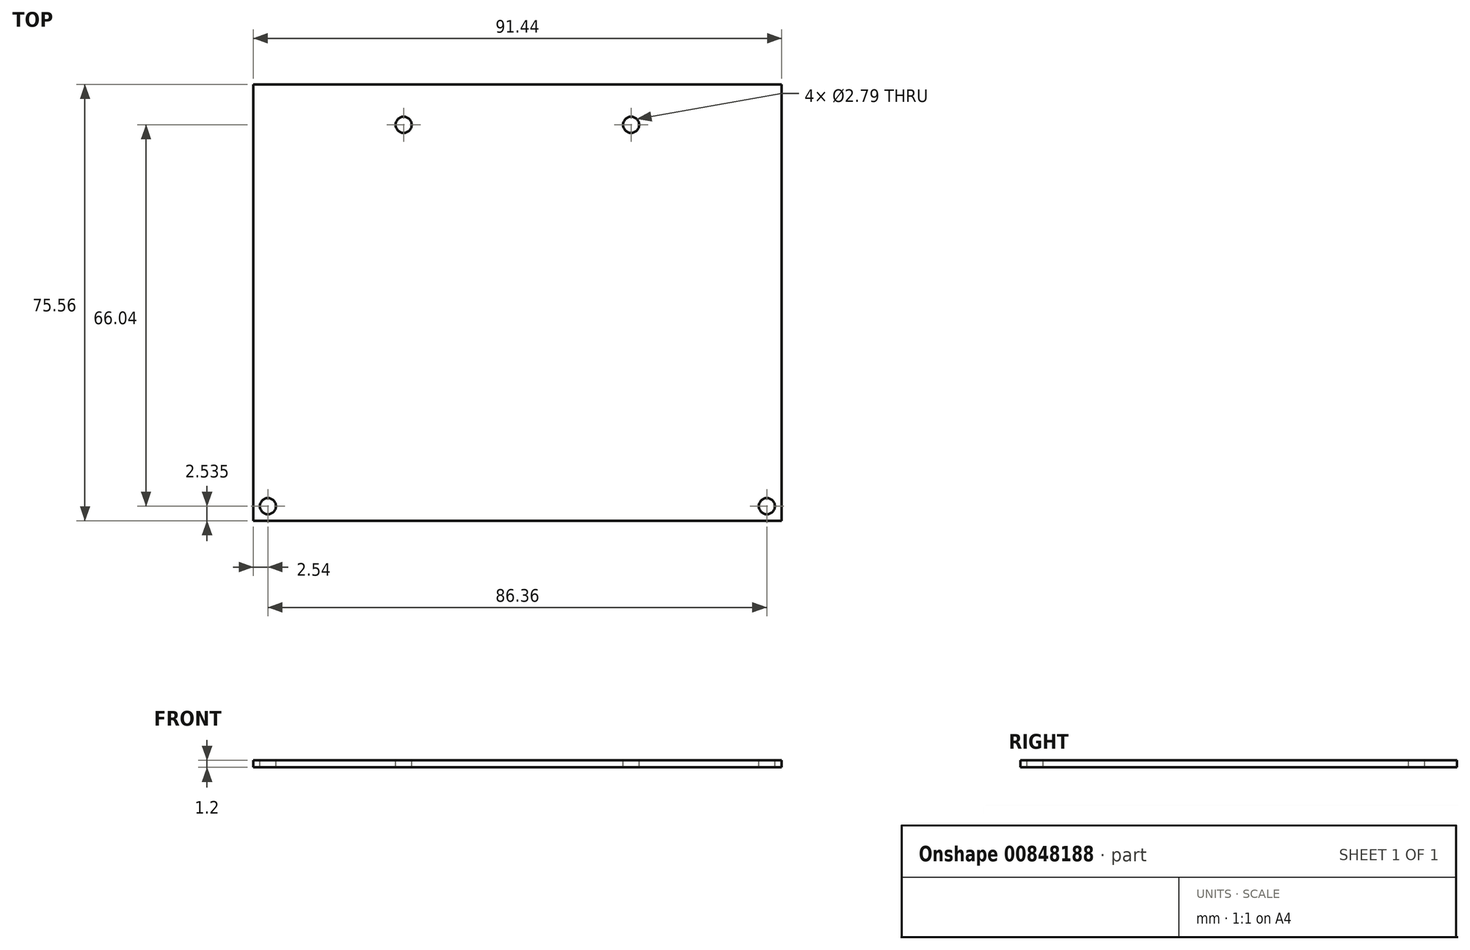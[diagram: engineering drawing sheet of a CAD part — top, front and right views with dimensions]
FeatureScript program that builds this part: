
annotation { "Feature Type Name" : "Feature", "Feature Type Description" : "" }
export const myFeature = defineFeature(function(context is Context, id is Id, definition is map)
    precondition{}
    {
        {
            var Q0;
            Q0=qCreatedBy(makeId("Top.planeOp"),FACE);
            var sketch = newSketch(context, id + "F0", { "sketchPlane" : qUnion([Q0])});
            skLineSegment(sketch, "E0.bottom", {"start": v(0, 0) * mm, "end": v(91.44, 0) * mm});
            skLineSegment(sketch, "E0.top", {"start": v(0, -75.56) * mm, "end": v(91.44, -75.56) * mm});
            skLineSegment(sketch, "E0.left", {"start": v(0, 0) * mm, "end": v(0, -75.56) * mm});
            skLineSegment(sketch, "E0.right", {"start": v(91.44, 0) * mm, "end": v(91.44, -75.56) * mm});
            skSolve(sketch);
        }
        {
            var Q0;
            Q0 = qSketchRegion(id + "F0", true);
            extrude(context, id + "F1", {"entities" : qUnion([Q0]), "depth" : 1.2 * mm, "offsetDistance" : 25.4 * mm});
        }
        {
            var Q0;
            Q0=makeQuery(id+"F1.opExtrude","CAP_FACE",FACE,{"disambiguationData":[OSD([sQuery(id+"F0.wireOp",EDGE,"E0.bottom"),sQuery(id+"F0.wireOp",EDGE,"E0.top"),sQuery(id+"F0.wireOp",EDGE,"E0.left"),sQuery(id+"F0.wireOp",EDGE,"E0.right")])],"isStart":false});
            var sketch = newSketch(context, id + "F2", { "sketchPlane" : qUnion([Q0])});
            skCircle(sketch, "E1", {"center": v(2.54, -73.02) * mm, "radius": 1.4 * mm});
            skCircle(sketch, "E2", {"center": v(88.9, -73.02) * mm, "radius": 1.4 * mm});
            skCircle(sketch, "E3", {"center": v(26.04, -6.98) * mm, "radius": 1.4 * mm});
            skLineSegment(sketch, "E4", {"start": v(0, -75.56) * mm, "end": v(91.44, -75.56) * mm, "construction": true});
            skCircle(sketch, "E5", {"center": v(65.4, -6.98) * mm, "radius": 1.4 * mm});
            skSolve(sketch);
        }
        {
            var Q0;
            Q0 = qSketchRegion(id + "F2", true);
            extrude(context, id + "F3", {"entities" : qUnion([Q0]), "operationType" : NewBodyOperationType.REMOVE, "oppositeDirection" : true, "depth" : 25.4 * mm, "offsetDistance" : 25.4 * mm});
        }
    });
